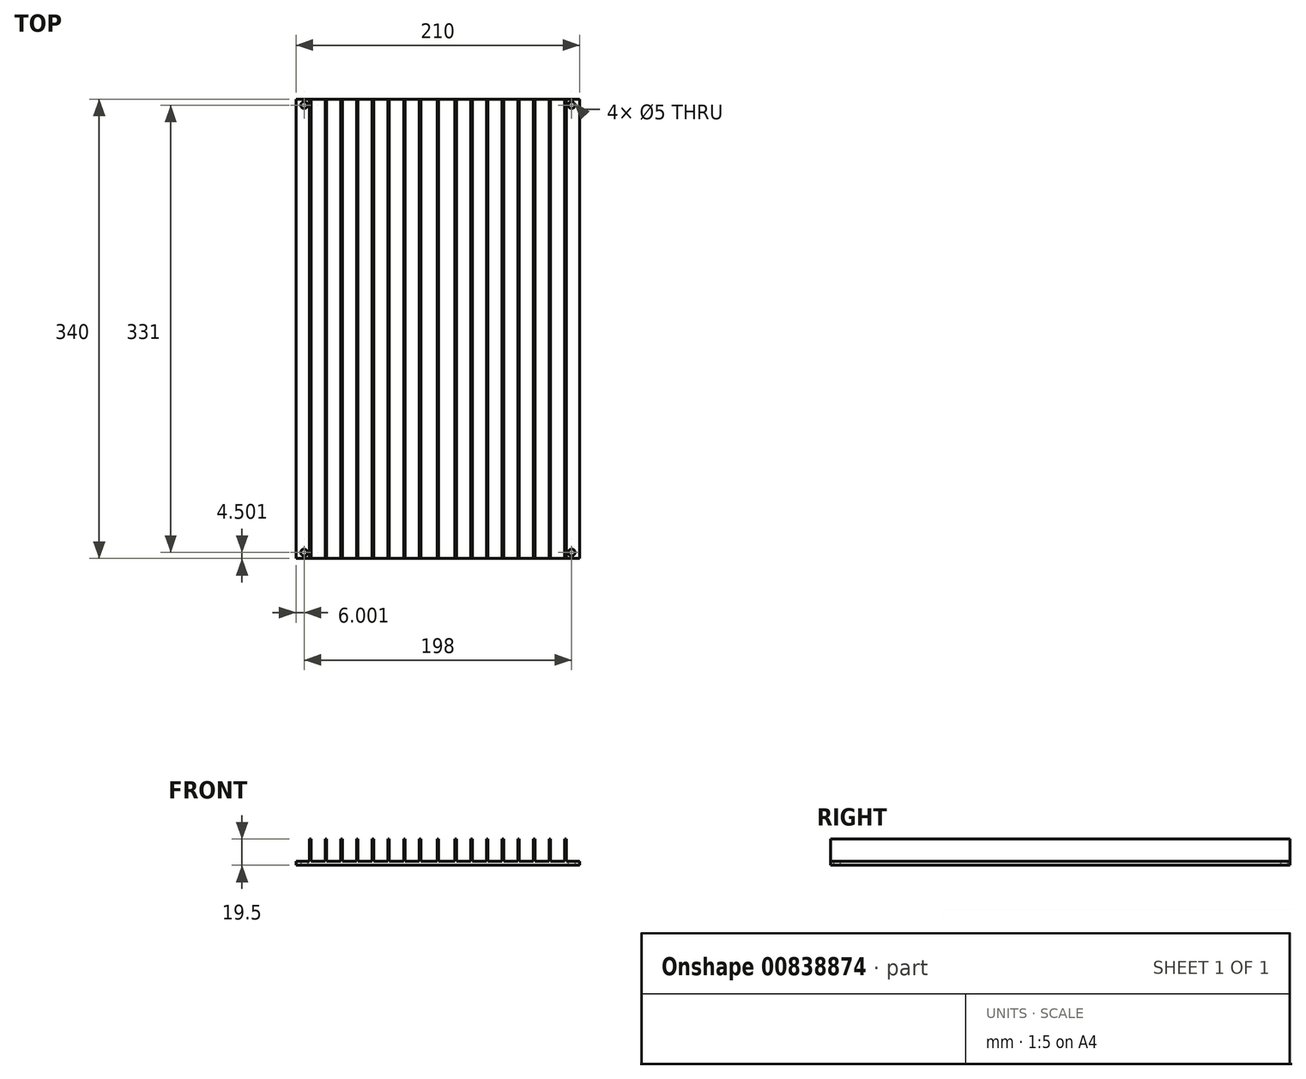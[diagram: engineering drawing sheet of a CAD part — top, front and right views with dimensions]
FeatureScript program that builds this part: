
annotation { "Feature Type Name" : "Feature", "Feature Type Description" : "" }
export const myFeature = defineFeature(function(context is Context, id is Id, definition is map)
    precondition{}
    {
        {
            var Q0;
            Q0=qCreatedBy(makeId("Top.planeOp"),FACE);
            var sketch = newSketch(context, id + "F0", { "sketchPlane" : qUnion([Q0])});
            skLineSegment(sketch, "E0.bottom", {"start": v(-106.83, 167.2) * mm, "end": v(103.17, 167.2) * mm});
            skLineSegment(sketch, "E0.top", {"start": v(-106.83, -172.8) * mm, "end": v(103.17, -172.8) * mm});
            skLineSegment(sketch, "E0.left", {"start": v(-106.83, 167.2) * mm, "end": v(-106.83, -172.8) * mm});
            skLineSegment(sketch, "E0.right", {"start": v(103.17, 167.2) * mm, "end": v(103.17, -172.8) * mm});
            skCircle(sketch, "E1", {"center": v(-100.83, 162.7) * mm, "radius": 2.5 * mm});
            skCircle(sketch, "E2", {"center": v(97.17, 162.7) * mm, "radius": 2.5 * mm});
            skCircle(sketch, "E3", {"center": v(-100.83, -168.3) * mm, "radius": 2.5 * mm});
            skCircle(sketch, "E4", {"center": v(97.17, -168.3) * mm, "radius": 2.5 * mm});
            skSolve(sketch);
        }
        {
            var Q0;
            Q0=qCreatedBy(makeId("Front.planeOp"),FACE);
            var sketch = newSketch(context, id + "F1", { "sketchPlane" : qUnion([Q0])});
            skLineSegment(sketch, "E5.0", {"start": v(-96.83, 19.5) * mm, "end": v(-95.73, 19.5) * mm});
            skLineSegment(sketch, "E6", {"start": v(-96.83, 3) * mm, "end": v(-96.83, 19.5) * mm});
            skLineSegment(sketch, "E7", {"start": v(-95.73, 3) * mm, "end": v(-95.73, 19.5) * mm});
            skLineSegment(sketch, "E8", {"start": v(-85.23, 3) * mm, "end": v(-85.23, 19.5) * mm});
            skLineSegment(sketch, "E9", {"start": v(-84.13, 3) * mm, "end": v(-84.13, 19.5) * mm});
            skLineSegment(sketch, "E10", {"start": v(-73.63, 3) * mm, "end": v(-73.63, 19.5) * mm});
            skLineSegment(sketch, "E11", {"start": v(-72.53, 3) * mm, "end": v(-72.53, 19.5) * mm});
            skLineSegment(sketch, "E12", {"start": v(-62.03, 3) * mm, "end": v(-62.03, 19.5) * mm});
            skLineSegment(sketch, "E13", {"start": v(-60.93, 3) * mm, "end": v(-60.93, 19.5) * mm});
            skLineSegment(sketch, "E14", {"start": v(-50.43, 3) * mm, "end": v(-50.43, 19.5) * mm});
            skLineSegment(sketch, "E15", {"start": v(-49.33, 3) * mm, "end": v(-49.33, 19.5) * mm});
            skLineSegment(sketch, "E16", {"start": v(-38.83, 3) * mm, "end": v(-38.83, 19.5) * mm});
            skLineSegment(sketch, "E17", {"start": v(-37.73, 3) * mm, "end": v(-37.73, 19.5) * mm});
            skLineSegment(sketch, "E18", {"start": v(-27.23, 3) * mm, "end": v(-27.23, 19.5) * mm});
            skLineSegment(sketch, "E19", {"start": v(-26.13, 3) * mm, "end": v(-26.13, 19.5) * mm});
            skLineSegment(sketch, "E20", {"start": v(-15.63, 3) * mm, "end": v(-15.63, 19.5) * mm});
            skLineSegment(sketch, "E21", {"start": v(-14.53, 3) * mm, "end": v(-14.53, 19.5) * mm});
            skLineSegment(sketch, "E22.MirrorCS", {"start": v(10.87, 3) * mm, "end": v(10.87, 19.5) * mm});
            skLineSegment(sketch, "E23.MirrorCS", {"start": v(11.97, 3) * mm, "end": v(11.97, 19.5) * mm});
            skLineSegment(sketch, "E24.MirrorCS", {"start": v(22.47, 3) * mm, "end": v(22.47, 19.5) * mm});
            skLineSegment(sketch, "E25.MirrorCS", {"start": v(23.57, 3) * mm, "end": v(23.57, 19.5) * mm});
            skLineSegment(sketch, "E26.MirrorCS", {"start": v(34.07, 3) * mm, "end": v(34.07, 19.5) * mm});
            skLineSegment(sketch, "E27.MirrorCS", {"start": v(35.17, 3) * mm, "end": v(35.17, 19.5) * mm});
            skLineSegment(sketch, "E28.MirrorCS", {"start": v(45.67, 3) * mm, "end": v(45.67, 19.5) * mm});
            skLineSegment(sketch, "E29.MirrorCS", {"start": v(46.77, 3) * mm, "end": v(46.77, 19.5) * mm});
            skLineSegment(sketch, "E30.MirrorCS", {"start": v(57.27, 3) * mm, "end": v(57.27, 19.5) * mm});
            skLineSegment(sketch, "E31.MirrorCS", {"start": v(58.37, 3) * mm, "end": v(58.37, 19.5) * mm});
            skLineSegment(sketch, "E32.MirrorCS", {"start": v(68.87, 3) * mm, "end": v(68.87, 19.5) * mm});
            skLineSegment(sketch, "E33.MirrorCS", {"start": v(69.97, 3) * mm, "end": v(69.97, 19.5) * mm});
            skLineSegment(sketch, "E34.MirrorCS", {"start": v(80.47, 3) * mm, "end": v(80.47, 19.5) * mm});
            skLineSegment(sketch, "E35.MirrorCS", {"start": v(81.57, 3) * mm, "end": v(81.57, 19.5) * mm});
            skLineSegment(sketch, "E36.MirrorCS", {"start": v(92.07, 3) * mm, "end": v(92.07, 19.5) * mm});
            skLineSegment(sketch, "E37.MirrorCS", {"start": v(93.17, 3) * mm, "end": v(93.17, 19.5) * mm});
            skLineSegment(sketch, "E38", {"start": v(-2.38, 3) * mm, "end": v(-2.38, 19.5) * mm});
            skLineSegment(sketch, "E39", {"start": v(-1.28, 3) * mm, "end": v(-1.28, 19.5) * mm});
            skLineSegment(sketch, "E40.trimOffspring", {"start": v(-85.23, 19.5) * mm, "end": v(-84.13, 19.5) * mm});
            skLineSegment(sketch, "E41.trimOffspring", {"start": v(-73.63, 19.5) * mm, "end": v(-72.53, 19.5) * mm});
            skLineSegment(sketch, "E42.trimOffspring", {"start": v(-62.03, 19.5) * mm, "end": v(-60.93, 19.5) * mm});
            skLineSegment(sketch, "E43.trimOffspring", {"start": v(-50.43, 19.5) * mm, "end": v(-49.33, 19.5) * mm});
            skLineSegment(sketch, "E44.trimOffspring", {"start": v(-38.83, 19.5) * mm, "end": v(-37.73, 19.5) * mm});
            skLineSegment(sketch, "E45.trimOffspring", {"start": v(-27.23, 19.5) * mm, "end": v(-26.13, 19.5) * mm});
            skLineSegment(sketch, "E46.trimOffspring", {"start": v(-15.63, 19.5) * mm, "end": v(-14.53, 19.5) * mm});
            skLineSegment(sketch, "E47.trimOffspring", {"start": v(-2.38, 19.5) * mm, "end": v(-1.28, 19.5) * mm});
            skLineSegment(sketch, "E48.trimOffspring", {"start": v(10.87, 19.5) * mm, "end": v(11.97, 19.5) * mm});
            skLineSegment(sketch, "E49.trimOffspring", {"start": v(22.47, 19.5) * mm, "end": v(23.57, 19.5) * mm});
            skLineSegment(sketch, "E50.trimOffspring", {"start": v(34.07, 19.5) * mm, "end": v(35.17, 19.5) * mm});
            skLineSegment(sketch, "E51.trimOffspring", {"start": v(45.67, 19.5) * mm, "end": v(46.77, 19.5) * mm});
            skLineSegment(sketch, "E52.trimOffspring", {"start": v(57.27, 19.5) * mm, "end": v(58.37, 19.5) * mm});
            skLineSegment(sketch, "E53.trimOffspring", {"start": v(68.87, 19.5) * mm, "end": v(69.97, 19.5) * mm});
            skLineSegment(sketch, "E54.trimOffspring", {"start": v(80.47, 19.5) * mm, "end": v(81.57, 19.5) * mm});
            skLineSegment(sketch, "E55.trimOffspring", {"start": v(92.07, 19.5) * mm, "end": v(93.17, 19.5) * mm});
            skLineSegment(sketch, "E56", {"start": v(-96.83, 3) * mm, "end": v(-95.73, 3) * mm});
            skLineSegment(sketch, "E57", {"start": v(-85.23, 3) * mm, "end": v(-84.13, 3) * mm});
            skLineSegment(sketch, "E58", {"start": v(-73.63, 3) * mm, "end": v(-72.53, 3) * mm});
            skLineSegment(sketch, "E59", {"start": v(-62.03, 3) * mm, "end": v(-60.93, 3) * mm});
            skLineSegment(sketch, "E60", {"start": v(-50.43, 3) * mm, "end": v(-49.33, 3) * mm});
            skLineSegment(sketch, "E61", {"start": v(-38.83, 3) * mm, "end": v(-37.73, 3) * mm});
            skLineSegment(sketch, "E62", {"start": v(-27.23, 3) * mm, "end": v(-26.13, 3) * mm});
            skLineSegment(sketch, "E63", {"start": v(-15.63, 3) * mm, "end": v(-14.53, 3) * mm});
            skLineSegment(sketch, "E64", {"start": v(-2.38, 3) * mm, "end": v(-1.28, 3) * mm});
            skLineSegment(sketch, "E65", {"start": v(10.87, 3) * mm, "end": v(11.97, 3) * mm});
            skLineSegment(sketch, "E66", {"start": v(22.47, 3) * mm, "end": v(23.57, 3) * mm});
            skLineSegment(sketch, "E67", {"start": v(34.07, 3) * mm, "end": v(35.17, 3) * mm});
            skLineSegment(sketch, "E68", {"start": v(45.67, 3) * mm, "end": v(46.77, 3) * mm});
            skLineSegment(sketch, "E69", {"start": v(57.27, 3) * mm, "end": v(58.37, 3) * mm});
            skLineSegment(sketch, "E70", {"start": v(68.87, 3) * mm, "end": v(69.97, 3) * mm});
            skLineSegment(sketch, "E71", {"start": v(80.47, 3) * mm, "end": v(81.57, 3) * mm});
            skLineSegment(sketch, "E72", {"start": v(92.07, 3) * mm, "end": v(93.17, 3) * mm});
            skSolve(sketch);
        }
        {
            var Q0;
            Q0 = qSketchRegion(id + "F0", true);
            extrude(context, id + "F2", {"entities" : qUnion([Q0]), "depth" : 3 * mm, "offsetDistance" : 25 * mm});
        }
        {
            var Q0;
            Q0 = qSketchRegion(id + "F1", true);
            extrude(context, id + "F3", {"entities" : qUnion([Q0]), "operationType" : NewBodyOperationType.ADD, "depth" : 172.79 * mm, "offsetDistance" : 25 * mm});
        }
        {
            var Q0;
            Q0 = qSketchRegion(id + "F1", true);
            extrude(context, id + "F4", {"entities" : qUnion([Q0]), "operationType" : NewBodyOperationType.ADD, "oppositeDirection" : true, "depth" : 167.2 * mm, "offsetDistance" : 25 * mm});
        }
    });
